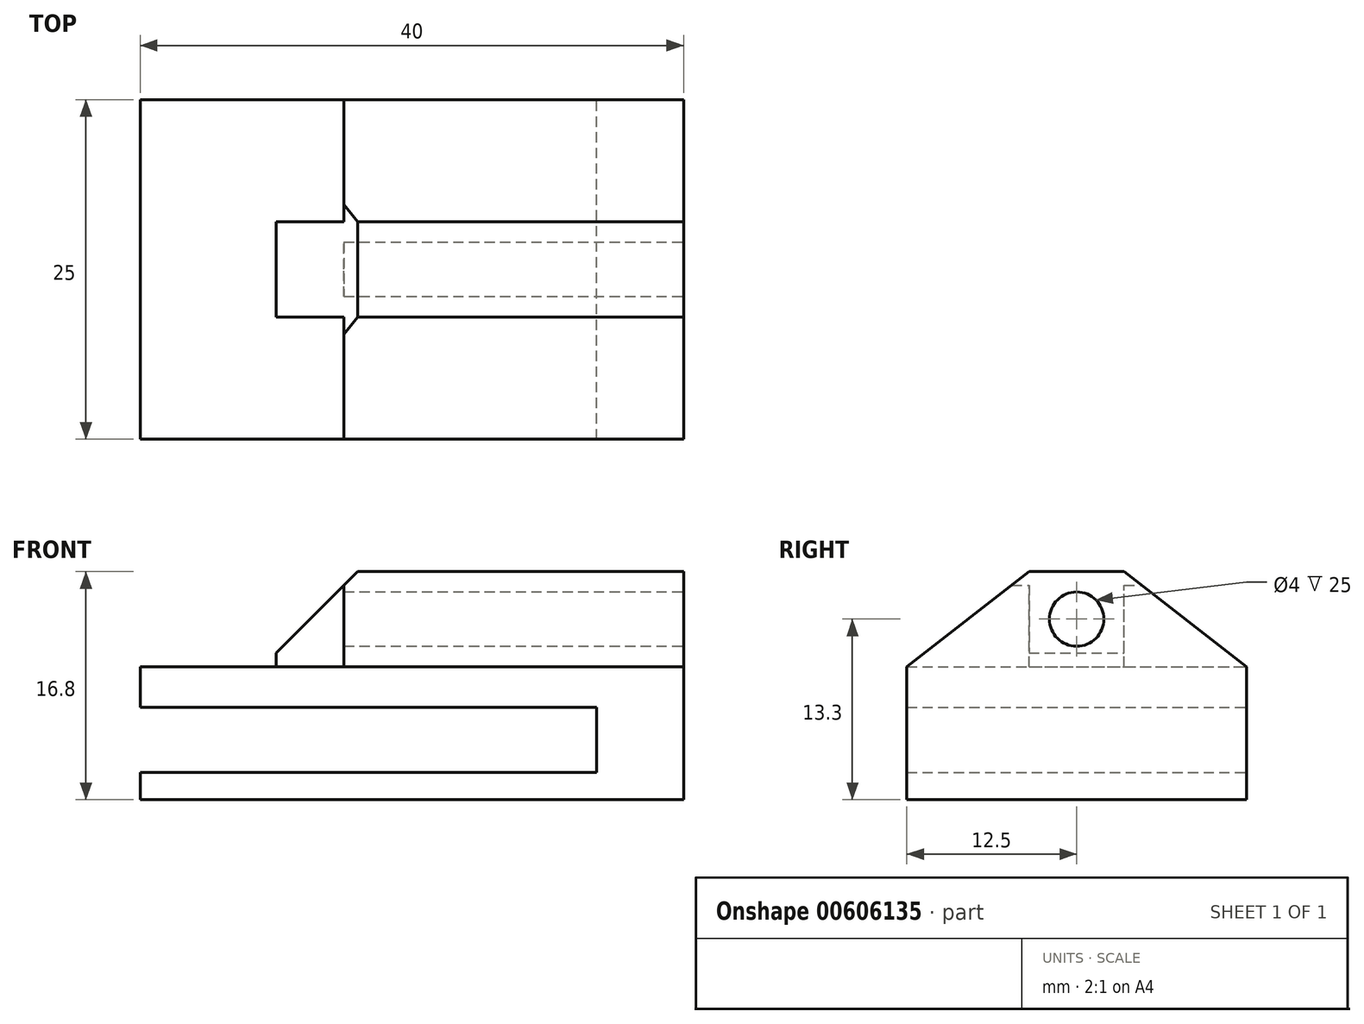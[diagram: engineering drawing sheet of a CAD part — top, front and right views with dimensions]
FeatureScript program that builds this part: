
annotation { "Feature Type Name" : "Feature", "Feature Type Description" : "" }
export const myFeature = defineFeature(function(context is Context, id is Id, definition is map)
    precondition{}
    {
        {
            var Q0;
            Q0=qCreatedBy(makeId("Front.planeOp"),FACE);
            var sketch = newSketch(context, id + "F0", { "sketchPlane" : qUnion([Q0])});
            skLineSegment(sketch, "E0", {"start": v(0, 0) * mm, "end": v(0, 9.8) * mm});
            skLineSegment(sketch, "E1", {"start": v(0, 9.8) * mm, "end": v(-40, 9.8) * mm});
            skLineSegment(sketch, "E2", {"start": v(-40, 9.8) * mm, "end": v(-40, 6.8) * mm});
            skLineSegment(sketch, "E3", {"start": v(-40, 6.8) * mm, "end": v(-6.4, 6.8) * mm});
            skLineSegment(sketch, "E4", {"start": v(-6.4, 6.8) * mm, "end": v(-6.4, 2) * mm});
            skLineSegment(sketch, "E5", {"start": v(-6.4, 2) * mm, "end": v(-40, 2) * mm});
            skLineSegment(sketch, "E6", {"start": v(-40, 2) * mm, "end": v(-40, 0) * mm});
            skLineSegment(sketch, "E7", {"start": v(-40, 0) * mm, "end": v(0, 0) * mm});
            skLineSegment(sketch, "E8.bottom", {"start": v(0, 9.8) * mm, "end": v(-30, 9.8) * mm});
            skLineSegment(sketch, "E8.top", {"start": v(0, 16.8) * mm, "end": v(-30, 16.8) * mm});
            skLineSegment(sketch, "E8.left", {"start": v(0, 9.8) * mm, "end": v(0, 16.8) * mm});
            skLineSegment(sketch, "E8.right", {"start": v(-30, 9.8) * mm, "end": v(-30, 16.8) * mm});
            skSolve(sketch);
        }
        {
            var Q0;
            {var subQ3=sQuery(id+"F0.wireOp",EDGE,"E0");Q0=makeQuery(id+"F0.imprint","IMPRINT",FACE,{"disambiguationData":[TD([[makeQuery(id+"F0.imprint","IMPRINT",EDGE,{"derivedFrom":subQ3}),1.0]])]});}
            var Q1;
            Q1=makeQuery(id+"F0.imprint","IMPRINT",FACE,{"disambiguationData":[TD([[makeQuery(id+"F0.imprint","IMPRINT",EDGE,{"derivedFrom":sQuery(id+"F0.wireOp",EDGE,"E8.top")}),1.0]])]});
            extrude(context, id + "F1", {"entities" : qUnion([Q0, Q1]), "depth" : 25 * mm, "offsetDistance" : 25 * mm});
        }
        {
            var Q0;
            Q0=makeQuery(id+"F1.opExtrude","SWEPT_FACE",FACE,{"disambiguationData":[OSD([sQuery(id+"F0.wireOp",EDGE,"E8.top")])]});
            var sketch = newSketch(context, id + "F2", { "sketchPlane" : qUnion([Q0])});
            skLineSegment(sketch, "E9.bottom", {"start": v(0, 0) * mm, "end": v(-30, 0) * mm});
            skLineSegment(sketch, "E9.top", {"start": v(0, -9) * mm, "end": v(-30, -9) * mm});
            skLineSegment(sketch, "E9.left", {"start": v(0, 0) * mm, "end": v(0, -9) * mm});
            skLineSegment(sketch, "E9.right", {"start": v(-30, 0) * mm, "end": v(-30, -9) * mm});
            skLineSegment(sketch, "E10.bottom", {"start": v(0, -25) * mm, "end": v(-30, -25) * mm});
            skLineSegment(sketch, "E10.top", {"start": v(0, -16) * mm, "end": v(-30, -16) * mm});
            skLineSegment(sketch, "E10.left", {"start": v(0, -25) * mm, "end": v(0, -16) * mm});
            skLineSegment(sketch, "E10.right", {"start": v(-30, -25) * mm, "end": v(-30, -16) * mm});
            skSolve(sketch);
        }
        {
            var Q0;
            Q0=makeQuery(id+"F2.imprint","IMPRINT",FACE,{"disambiguationData":[TD([[makeQuery(id+"F2.imprint","IMPRINT",EDGE,{"derivedFrom":sQuery(id+"F2.wireOp",EDGE,"E9.bottom")}),1.0]])]});
            var Q1;
            Q1=makeQuery(id+"F2.imprint","IMPRINT",FACE,{"disambiguationData":[TD([[makeQuery(id+"F2.imprint","IMPRINT",EDGE,{"derivedFrom":sQuery(id+"F2.wireOp",EDGE,"E10.bottom")}),-1.0]])]});
            extrude(context, id + "F3", {"entities" : qUnion([Q0, Q1]), "operationType" : NewBodyOperationType.REMOVE, "oppositeDirection" : true, "depth" : 7 * mm, "offsetDistance" : 25 * mm});
        }
        {
            var Q0;
            Q0=makeQuery(id+"F1.opExtrude","SWEPT_FACE",FACE,{"disambiguationData":[OSD([sQuery(id+"F0.wireOp",EDGE,"E0"),sQuery(id+"F0.wireOp",EDGE,"E8.left")])]});
            var sketch = newSketch(context, id + "F4", { "sketchPlane" : qUnion([Q0])});
            skLineSegment(sketch, "E11", {"start": v(-16, 16.8) * mm, "end": v(-9, 9.8) * mm, "construction": true});
            skLineSegment(sketch, "E12", {"start": v(-9, 16.8) * mm, "end": v(-16, 9.8) * mm, "construction": true});
            skPoint(sketch, "E13", {"position": v(-12.5, 13.3) * mm});
            skCircle(sketch, "E14", {"center": v(-12.5, 13.3) * mm, "radius": 2 * mm});
            skSolve(sketch);
        }
        {
            var Q0;
            Q0=makeQuery(id+"F4.imprint","IMPRINT",FACE,{"disambiguationData":[TD([[makeQuery(id+"F4.imprint","IMPRINT",EDGE,{"derivedFrom":sQuery(id+"F4.wireOp",EDGE,"E14")}),1.0]])]});
            extrude(context, id + "F5", {"entities" : qUnion([Q0]), "operationType" : NewBodyOperationType.REMOVE, "oppositeDirection" : true, "depth" : 25 * mm, "offsetDistance" : 25 * mm});
        }
        {
            var Q0;
            Q0=makeQuery(id+"F1.opExtrude","SWEPT_FACE",FACE,{"disambiguationData":[OSD([sQuery(id+"F0.wireOp",EDGE,"E0"),sQuery(id+"F0.wireOp",EDGE,"E8.left")])]});
            var sketch = newSketch(context, id + "F6", { "sketchPlane" : qUnion([Q0])});
            skLineSegment(sketch, "E15", {"start": v(-25, 9.8) * mm, "end": v(-16, 16.8) * mm});
            skLineSegment(sketch, "E16", {"start": v(-16, 16.8) * mm, "end": v(-9, 16.8) * mm});
            skLineSegment(sketch, "E17", {"start": v(-9, 16.8) * mm, "end": v(0, 9.8) * mm});
            skLineSegment(sketch, "E18", {"start": v(0, 9.8) * mm, "end": v(-25, 9.8) * mm});
            skSolve(sketch);
        }
        {
            var Q0;
            {var subQ0=sQuery(id+"F6.wireOp",EDGE,"E15");Q0=makeQuery(id+"F6.imprint","IMPRINT",FACE,{"disambiguationData":[TD([[makeQuery(id+"F6.imprint","IMPRINT",EDGE,{"derivedFrom":subQ0}),-1.0]])]});}
            var Q1;
            {var subQ0=sQuery(id+"F6.wireOp",EDGE,"E17");Q1=makeQuery(id+"F6.imprint","IMPRINT",FACE,{"disambiguationData":[TD([[makeQuery(id+"F6.imprint","IMPRINT",EDGE,{"derivedFrom":subQ0}),-1.0]])]});}
            extrude(context, id + "F7", {"entities" : qUnion([Q0, Q1]), "operationType" : NewBodyOperationType.ADD, "oppositeDirection" : true, "depth" : 25 * mm, "offsetDistance" : 25 * mm});
        }
        {
            var Q0;
            Q0=makeQuery(id+"F1.opExtrude","SWEPT_EDGE",EDGE,{"disambiguationData":[OSD([sQuery(id+"F0.wireOp",EDGE,"E8.top"),sQuery(id+"F0.wireOp",EDGE,"E8.right")])]});
            chamfer(context, id + "F8", {"entities" : qUnion([Q0]), "width" : 6 * mm, "tangentPropagation" : true});
        }
    });
